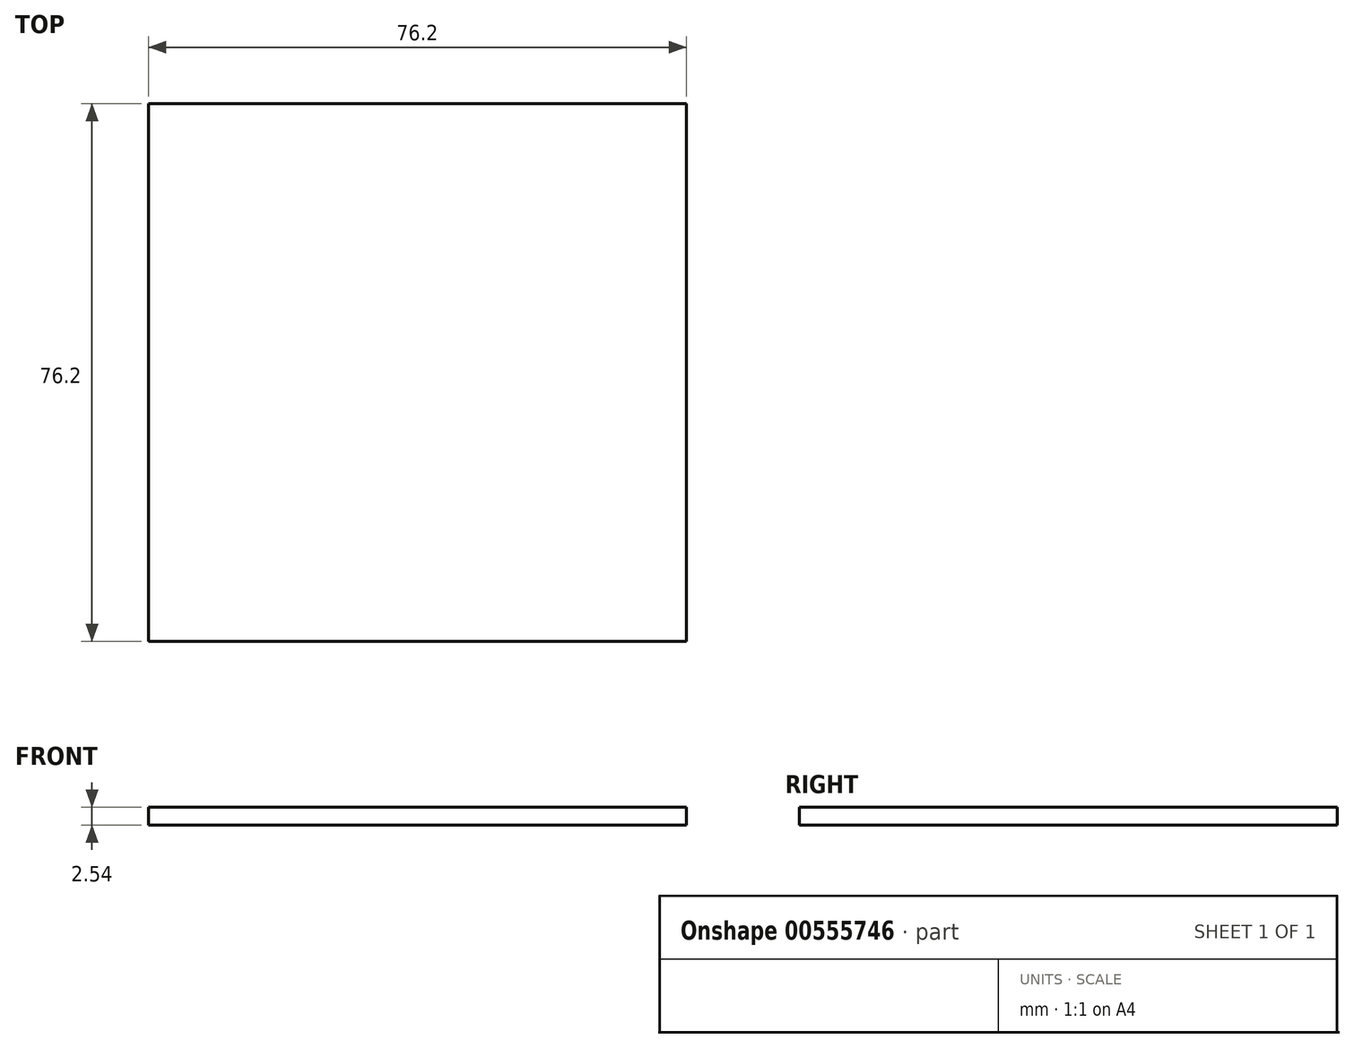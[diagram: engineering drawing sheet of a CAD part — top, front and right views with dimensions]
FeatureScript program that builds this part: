
annotation { "Feature Type Name" : "Feature", "Feature Type Description" : "" }
export const myFeature = defineFeature(function(context is Context, id is Id, definition is map)
    precondition{}
    {
        {
            var Q0;
            Q0=qCreatedBy(makeId("Top.planeOp"),FACE);
            var sketch = newSketch(context, id + "F0", { "sketchPlane" : qUnion([Q0])});
            skLineSegment(sketch, "E0.bottom", {"start": v(0, 0) * mm, "end": v(76.2, 0) * mm});
            skLineSegment(sketch, "E0.top", {"start": v(0, -76.2) * mm, "end": v(76.2, -76.2) * mm});
            skLineSegment(sketch, "E0.left", {"start": v(0, 0) * mm, "end": v(0, -76.2) * mm});
            skLineSegment(sketch, "E0.right", {"start": v(76.2, 0) * mm, "end": v(76.2, -76.2) * mm});
            skSolve(sketch);
        }
        {
            var Q0;
            Q0=makeQuery(id+"F0.imprint","IMPRINT",FACE,{"disambiguationData":[TD([[makeQuery(id+"F0.imprint","IMPRINT",EDGE,{"derivedFrom":sQuery(id+"F0.wireOp",EDGE,"E0.bottom")}),-1.0]])]});
            extrude(context, id + "F1", {"entities" : qUnion([Q0]), "depth" : 2.54 * mm, "offsetDistance" : 25.4 * mm});
        }
    });
